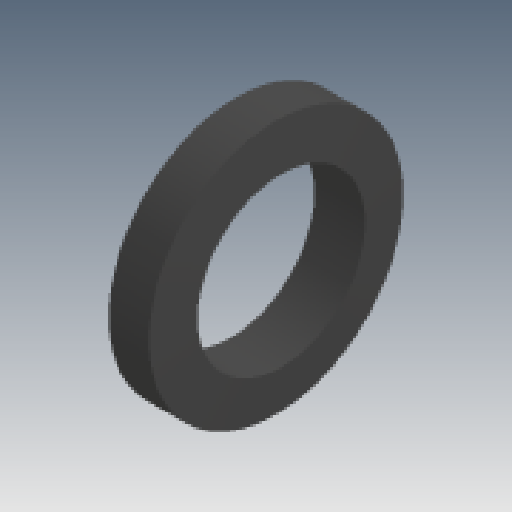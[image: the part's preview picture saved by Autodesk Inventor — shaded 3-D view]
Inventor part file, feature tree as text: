
AUTODESK INVENTOR PART (.ipt)
format: ipt  version: 2025 (Build 290162000, 162)  size: 98,304 bytes
history: native  units: mm
features: other x2, revolve x1, sketch x1, reference x1
ambient origin geometry x8: Origin, YZ Plane, XZ Plane, XY Plane, X Axis, Y Axis, Z Axis, Center Point
bodies: Body1 (feature_tree)
feature tree (5):
  revolve  "旋转2"  Angle=90.0deg
  sketch  "草图2"  dims[d3=12.5mm d4=90.0deg]
  reference  "参考2"
  other  "齿轮箱.iam"
  other  "高速轴承透盖"
